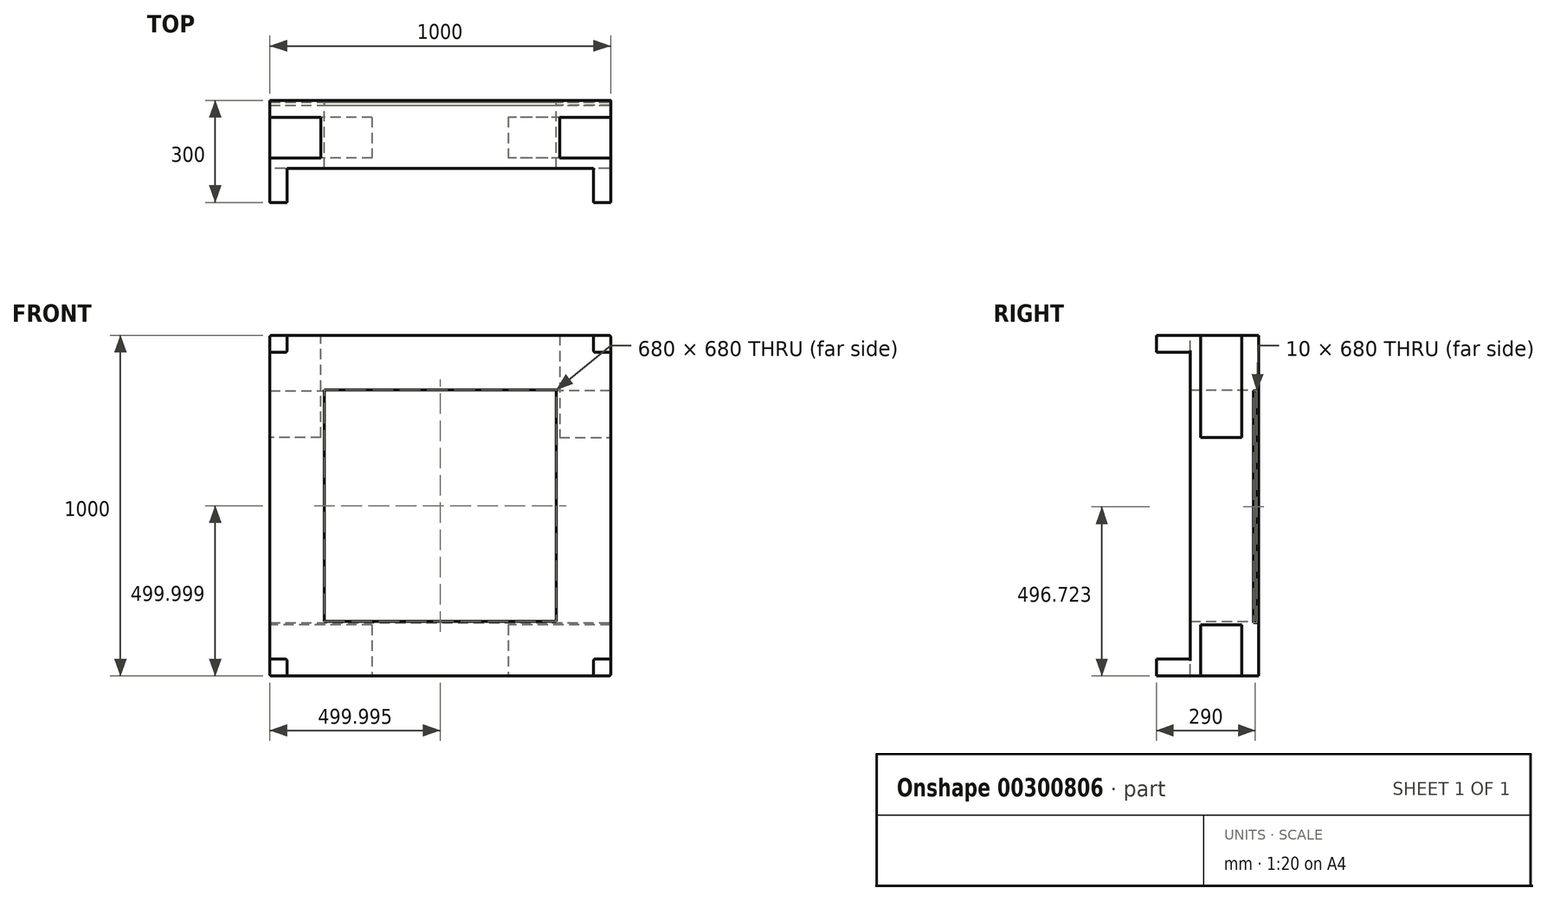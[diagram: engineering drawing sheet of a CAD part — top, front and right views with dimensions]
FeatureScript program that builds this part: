
annotation { "Feature Type Name" : "Feature", "Feature Type Description" : "" }
export const myFeature = defineFeature(function(context is Context, id is Id, definition is map)
    precondition{}
    {
        {
            var Q0;
            Q0=qCreatedBy(makeId("Front.planeOp"),FACE);
            var sketch = newSketch(context, id + "F0", { "sketchPlane" : qUnion([Q0])});
            skLineSegment(sketch, "E0.bottom", {"start": v(-49.23, 948.9) * mm, "end": v(950.77, 948.9) * mm});
            skLineSegment(sketch, "E0.top", {"start": v(-49.23, -51.1) * mm, "end": v(950.77, -51.1) * mm});
            skLineSegment(sketch, "E0.left", {"start": v(-49.23, 948.9) * mm, "end": v(-49.23, -51.1) * mm});
            skLineSegment(sketch, "E0.right", {"start": v(950.77, 948.9) * mm, "end": v(950.77, -51.1) * mm});
            skSolve(sketch);
        }
        {
            var Q0;
            Q0 = qSketchRegion(id + "F0", true);
            extrude(context, id + "F1", {"entities" : qUnion([Q0]), "depth" : 300 * mm});
        }
        {
            var Q0;
            Q0=makeQuery(id+"F1.opExtrude","SWEPT_FACE",FACE,{"disambiguationData":[OSD([sQuery(id+"F0.wireOp",EDGE,"E0.bottom")])]});
            var sketch = newSketch(context, id + "F2", { "sketchPlane" : qUnion([Q0])});
            skLineSegment(sketch, "E1.bottom", {"start": v(0.77, -300) * mm, "end": v(900.77, -300) * mm});
            skLineSegment(sketch, "E1.top", {"start": v(0.77, -200) * mm, "end": v(900.77, -200) * mm});
            skLineSegment(sketch, "E1.left", {"start": v(0.77, -300) * mm, "end": v(0.77, -200) * mm});
            skLineSegment(sketch, "E1.right", {"start": v(900.77, -300) * mm, "end": v(900.77, -200) * mm});
            skSolve(sketch);
        }
        {
            var Q0;
            Q0 = qSketchRegion(id + "F2", true);
            extrude(context, id + "F3", {"entities" : qUnion([Q0]), "operationType" : NewBodyOperationType.REMOVE, "endBound" : BoundingType.THROUGH_ALL, "oppositeDirection" : true, "depth" : 100 * mm});
        }
        {
            var Q0;
            Q0=makeQuery(id+"F1.opExtrude","SWEPT_FACE",FACE,{"disambiguationData":[OSD([sQuery(id+"F0.wireOp",EDGE,"E0.left")])]});
            var sketch = newSketch(context, id + "F4", { "sketchPlane" : qUnion([Q0])});
            skLineSegment(sketch, "E2.bottom", {"start": v(300, -1.1) * mm, "end": v(200, -1.1) * mm});
            skLineSegment(sketch, "E2.top", {"start": v(300, 898.9) * mm, "end": v(200, 898.9) * mm});
            skLineSegment(sketch, "E2.left", {"start": v(300, -1.1) * mm, "end": v(300, 898.9) * mm});
            skLineSegment(sketch, "E2.right", {"start": v(200, -1.1) * mm, "end": v(200, 898.9) * mm});
            skSolve(sketch);
        }
        {
            var Q0;
            Q0 = qSketchRegion(id + "F4", true);
            extrude(context, id + "F5", {"entities" : qUnion([Q0]), "operationType" : NewBodyOperationType.REMOVE, "endBound" : BoundingType.THROUGH_ALL, "oppositeDirection" : true, "depth" : 25 * mm});
        }
        {
            var Q0;
            Q0=makeQuery(id+"F1.opExtrude","SWEPT_FACE",FACE,{"disambiguationData":[OSD([sQuery(id+"F0.wireOp",EDGE,"E0.top")])]});
            var sketch = newSketch(context, id + "F6", { "sketchPlane" : qUnion([Q0])});
            skLineSegment(sketch, "E3.bottom", {"start": v(250.77, 50) * mm, "end": v(-49.23, 50) * mm});
            skLineSegment(sketch, "E3.top", {"start": v(250.77, 170) * mm, "end": v(-49.23, 170) * mm});
            skLineSegment(sketch, "E3.left", {"start": v(250.77, 50) * mm, "end": v(250.77, 170) * mm});
            skLineSegment(sketch, "E3.right", {"start": v(-49.23, 50) * mm, "end": v(-49.23, 170) * mm});
            skSolve(sketch);
        }
        {
            var Q0;
            Q0 = qSketchRegion(id + "F6", true);
            extrude(context, id + "F7", {"entities" : qUnion([Q0]), "operationType" : NewBodyOperationType.REMOVE, "oppositeDirection" : true, "depth" : 150 * mm});
        }
        {
            var Q0;
            Q0=makeQuery(id+"F1.opExtrude","SWEPT_FACE",FACE,{"disambiguationData":[OSD([sQuery(id+"F0.wireOp",EDGE,"E0.top")])]});
            var sketch = newSketch(context, id + "F8", { "sketchPlane" : qUnion([Q0])});
            skLineSegment(sketch, "E4.bottom", {"start": v(950.77, 50) * mm, "end": v(650.77, 50) * mm});
            skLineSegment(sketch, "E4.top", {"start": v(950.77, 170) * mm, "end": v(650.77, 170) * mm});
            skLineSegment(sketch, "E4.left", {"start": v(950.77, 50) * mm, "end": v(950.77, 170) * mm});
            skLineSegment(sketch, "E4.right", {"start": v(650.77, 50) * mm, "end": v(650.77, 170) * mm});
            skSolve(sketch);
        }
        {
            var Q0;
            Q0 = qSketchRegion(id + "F8", true);
            extrude(context, id + "F9", {"entities" : qUnion([Q0]), "operationType" : NewBodyOperationType.REMOVE, "oppositeDirection" : true, "depth" : 150 * mm});
        }
        {
            var Q0;
            Q0=makeQuery(id+"F1.opExtrude","SWEPT_FACE",FACE,{"disambiguationData":[OSD([sQuery(id+"F0.wireOp",EDGE,"E0.right")])]});
            var sketch = newSketch(context, id + "F10", { "sketchPlane" : qUnion([Q0])});
            skLineSegment(sketch, "E5.bottom", {"start": v(-50, 948.9) * mm, "end": v(-170, 948.9) * mm});
            skLineSegment(sketch, "E5.top", {"start": v(-50, 648.9) * mm, "end": v(-170, 648.9) * mm});
            skLineSegment(sketch, "E5.left", {"start": v(-50, 948.9) * mm, "end": v(-50, 648.9) * mm});
            skLineSegment(sketch, "E5.right", {"start": v(-170, 948.9) * mm, "end": v(-170, 648.9) * mm});
            skSolve(sketch);
        }
        {
            var Q0;
            Q0 = qSketchRegion(id + "F10", true);
            extrude(context, id + "F11", {"entities" : qUnion([Q0]), "operationType" : NewBodyOperationType.REMOVE, "oppositeDirection" : true, "depth" : 150 * mm});
        }
        {
            var Q0;
            Q0=makeQuery(id+"F1.opExtrude","SWEPT_FACE",FACE,{"disambiguationData":[OSD([sQuery(id+"F0.wireOp",EDGE,"E0.left")])]});
            var sketch = newSketch(context, id + "F12", { "sketchPlane" : qUnion([Q0])});
            skLineSegment(sketch, "E6.bottom", {"start": v(50, 648.9) * mm, "end": v(170, 648.9) * mm});
            skLineSegment(sketch, "E6.top", {"start": v(50, 948.9) * mm, "end": v(170, 948.9) * mm});
            skLineSegment(sketch, "E6.left", {"start": v(50, 648.9) * mm, "end": v(50, 948.9) * mm});
            skLineSegment(sketch, "E6.right", {"start": v(170, 648.9) * mm, "end": v(170, 948.9) * mm});
            skSolve(sketch);
        }
        {
            var Q0;
            Q0 = qSketchRegion(id + "F12", true);
            extrude(context, id + "F13", {"entities" : qUnion([Q0]), "operationType" : NewBodyOperationType.REMOVE, "oppositeDirection" : true, "depth" : 150 * mm});
        }
        {
            var Q0;
            {var subQ0=sQuery(id+"F0.wireOp",EDGE,"E0.right");var subQ1=sQuery(id+"F0.wireOp",EDGE,"E0.top");Q0=makeQuery(id+"F9.boolean.opBoolean","SPLIT",EDGE,{"disambiguationData":[TD([makeQuery(id+"F9.opExtrude","SWEPT_FACE",FACE,{"disambiguationData":[OSD([sQuery(id+"F8.wireOp",EDGE,"E4.top")])]})])],"derivedFrom":makeQuery(id+"F1.opExtrude","SWEPT_EDGE",EDGE,{"disambiguationData":[OSD([subQ1,subQ0])]})});}
            var Q1;
            Q1=makeQuery(id+"F3.boolean.opBoolean","INTERSECT",EDGE,{"derivedFrom":[makeQuery(id+"F1.opExtrude","SWEPT_FACE",FACE,{"disambiguationData":[OSD([sQuery(id+"F0.wireOp",EDGE,"E0.top")])]}),makeQuery(id+"F3.opExtrude","SWEPT_FACE",FACE,{"disambiguationData":[OSD([sQuery(id+"F2.wireOp",EDGE,"E1.right")])]})]});
            var Q2;
            Q2=makeQuery(id+"F5.boolean.opBoolean","INTERSECT",EDGE,{"derivedFrom":[makeQuery(id+"F1.opExtrude","SWEPT_FACE",FACE,{"disambiguationData":[OSD([sQuery(id+"F0.wireOp",EDGE,"E0.right")])]}),makeQuery(id+"F5.opExtrude","SWEPT_FACE",FACE,{"disambiguationData":[OSD([sQuery(id+"F4.wireOp",EDGE,"E2.bottom")])]})]});
            var Q3;
            Q3=makeQuery(id+"F5.boolean.opBoolean","INTERSECT",EDGE,{"derivedFrom":[makeQuery(id+"F3.boolean.opBoolean","COPY",FACE,{"derivedFrom":makeQuery(id+"F3.opExtrude","SWEPT_FACE",FACE,{"disambiguationData":[OSD([sQuery(id+"F2.wireOp",EDGE,"E1.right")])]})}),makeQuery(id+"F5.opExtrude","SWEPT_FACE",FACE,{"disambiguationData":[OSD([sQuery(id+"F4.wireOp",EDGE,"E2.bottom")])]})]});
            var Q4;
            {var subQ0=sQuery(id+"F0.wireOp",EDGE,"E0.left");var subQ1=sQuery(id+"F0.wireOp",EDGE,"E0.top");Q4=makeQuery(id+"F7.boolean.opBoolean","SPLIT",EDGE,{"disambiguationData":[TD([makeQuery(id+"F7.opExtrude","SWEPT_FACE",FACE,{"disambiguationData":[OSD([sQuery(id+"F6.wireOp",EDGE,"E3.top")])]})])],"derivedFrom":makeQuery(id+"F1.opExtrude","SWEPT_EDGE",EDGE,{"disambiguationData":[OSD([subQ1,subQ0])]})});}
            var Q5;
            Q5=makeQuery(id+"F3.boolean.opBoolean","INTERSECT",EDGE,{"derivedFrom":[makeQuery(id+"F1.opExtrude","SWEPT_FACE",FACE,{"disambiguationData":[OSD([sQuery(id+"F0.wireOp",EDGE,"E0.top")])]}),makeQuery(id+"F3.opExtrude","SWEPT_FACE",FACE,{"disambiguationData":[OSD([sQuery(id+"F2.wireOp",EDGE,"E1.left")])]})]});
            var Q6;
            Q6=makeQuery(id+"F5.boolean.opBoolean","COPY",EDGE,{"derivedFrom":makeQuery(id+"F5.opExtrude","CAP_EDGE",EDGE,{"disambiguationData":[OSD([sQuery(id+"F4.wireOp",EDGE,"E2.bottom")])],"isStart":true})});
            var Q7;
            Q7=makeQuery(id+"F5.boolean.opBoolean","INTERSECT",EDGE,{"derivedFrom":[makeQuery(id+"F3.boolean.opBoolean","COPY",FACE,{"derivedFrom":makeQuery(id+"F3.opExtrude","SWEPT_FACE",FACE,{"disambiguationData":[OSD([sQuery(id+"F2.wireOp",EDGE,"E1.left")])]})}),makeQuery(id+"F5.opExtrude","SWEPT_FACE",FACE,{"disambiguationData":[OSD([sQuery(id+"F4.wireOp",EDGE,"E2.bottom")])]})]});
            var Q8;
            {var subQ0=sQuery(id+"F0.wireOp",EDGE,"E0.bottom");var subQ1=sQuery(id+"F0.wireOp",EDGE,"E0.left");Q8=makeQuery(id+"F13.boolean.opBoolean","SPLIT",EDGE,{"disambiguationData":[TD([makeQuery(id+"F13.opExtrude","SWEPT_FACE",FACE,{"disambiguationData":[OSD([sQuery(id+"F12.wireOp",EDGE,"E6.right")])]})])],"derivedFrom":makeQuery(id+"F1.opExtrude","SWEPT_EDGE",EDGE,{"disambiguationData":[OSD([subQ0,subQ1])]})});}
            var Q9;
            Q9=makeQuery(id+"F3.boolean.opBoolean","COPY",EDGE,{"derivedFrom":makeQuery(id+"F3.opExtrude","CAP_EDGE",EDGE,{"disambiguationData":[OSD([sQuery(id+"F2.wireOp",EDGE,"E1.left")])],"isStart":true})});
            var Q10;
            Q10=makeQuery(id+"F5.boolean.opBoolean","COPY",EDGE,{"derivedFrom":makeQuery(id+"F5.opExtrude","CAP_EDGE",EDGE,{"disambiguationData":[OSD([sQuery(id+"F4.wireOp",EDGE,"E2.top")])],"isStart":true})});
            var Q11;
            Q11=makeQuery(id+"F5.boolean.opBoolean","INTERSECT",EDGE,{"derivedFrom":[makeQuery(id+"F3.boolean.opBoolean","COPY",FACE,{"derivedFrom":makeQuery(id+"F3.opExtrude","SWEPT_FACE",FACE,{"disambiguationData":[OSD([sQuery(id+"F2.wireOp",EDGE,"E1.left")])]})}),makeQuery(id+"F5.opExtrude","SWEPT_FACE",FACE,{"disambiguationData":[OSD([sQuery(id+"F4.wireOp",EDGE,"E2.top")])]})]});
            var Q12;
            {var subQ0=sQuery(id+"F0.wireOp",EDGE,"E0.bottom");var subQ1=sQuery(id+"F0.wireOp",EDGE,"E0.right");Q12=makeQuery(id+"F11.boolean.opBoolean","SPLIT",EDGE,{"disambiguationData":[TD([makeQuery(id+"F11.opExtrude","SWEPT_FACE",FACE,{"disambiguationData":[OSD([sQuery(id+"F10.wireOp",EDGE,"E5.right")])]})])],"derivedFrom":makeQuery(id+"F1.opExtrude","SWEPT_EDGE",EDGE,{"disambiguationData":[OSD([subQ0,subQ1])]})});}
            var Q13;
            Q13=makeQuery(id+"F5.boolean.opBoolean","INTERSECT",EDGE,{"derivedFrom":[makeQuery(id+"F1.opExtrude","SWEPT_FACE",FACE,{"disambiguationData":[OSD([sQuery(id+"F0.wireOp",EDGE,"E0.right")])]}),makeQuery(id+"F5.opExtrude","SWEPT_FACE",FACE,{"disambiguationData":[OSD([sQuery(id+"F4.wireOp",EDGE,"E2.top")])]})]});
            var Q14;
            Q14=makeQuery(id+"F5.boolean.opBoolean","INTERSECT",EDGE,{"derivedFrom":[makeQuery(id+"F3.boolean.opBoolean","COPY",FACE,{"derivedFrom":makeQuery(id+"F3.opExtrude","SWEPT_FACE",FACE,{"disambiguationData":[OSD([sQuery(id+"F2.wireOp",EDGE,"E1.right")])]})}),makeQuery(id+"F5.opExtrude","SWEPT_FACE",FACE,{"disambiguationData":[OSD([sQuery(id+"F4.wireOp",EDGE,"E2.top")])]})]});
            var Q15;
            Q15=makeQuery(id+"F3.boolean.opBoolean","COPY",EDGE,{"derivedFrom":makeQuery(id+"F3.opExtrude","CAP_EDGE",EDGE,{"disambiguationData":[OSD([sQuery(id+"F2.wireOp",EDGE,"E1.right")])],"isStart":true})});
            fillet(context, id + "F14", {"entities" : qUnion([Q0, Q1, Q2, Q3, Q4, Q5, Q6, Q7, Q8, Q9, Q10, Q11, Q12, Q13, Q14, Q15]), "radius" : 5 * mm, "tangentPropagation" : true, "allowEdgeOverflow" : false});
        }
        {
            var Q0;
            {var subQ0=sQuery(id+"F0.wireOp",EDGE,"E0.bottom");var subQ1=sQuery(id+"F0.wireOp",EDGE,"E0.right");Q0=makeQuery(id+"F11.boolean.opBoolean","SPLIT",EDGE,{"disambiguationData":[TD([makeQuery(id+"F11.opExtrude","SWEPT_FACE",FACE,{"disambiguationData":[OSD([sQuery(id+"F10.wireOp",EDGE,"E5.left")])]})])],"derivedFrom":makeQuery(id+"F1.opExtrude","SWEPT_EDGE",EDGE,{"disambiguationData":[OSD([subQ0,subQ1])]})});}
            var Q1;
            {var subQ0=sQuery(id+"F0.wireOp",EDGE,"E0.right");var subQ1=sQuery(id+"F0.wireOp",EDGE,"E0.top");Q1=makeQuery(id+"F9.boolean.opBoolean","SPLIT",EDGE,{"disambiguationData":[TD([makeQuery(id+"F9.opExtrude","SWEPT_FACE",FACE,{"disambiguationData":[OSD([sQuery(id+"F8.wireOp",EDGE,"E4.bottom")])]})])],"derivedFrom":makeQuery(id+"F1.opExtrude","SWEPT_EDGE",EDGE,{"disambiguationData":[OSD([subQ1,subQ0])]})});}
            var Q2;
            {var subQ0=sQuery(id+"F0.wireOp",EDGE,"E0.left");var subQ1=sQuery(id+"F0.wireOp",EDGE,"E0.top");Q2=makeQuery(id+"F7.boolean.opBoolean","SPLIT",EDGE,{"disambiguationData":[TD([makeQuery(id+"F7.opExtrude","SWEPT_FACE",FACE,{"disambiguationData":[OSD([sQuery(id+"F6.wireOp",EDGE,"E3.bottom")])]})])],"derivedFrom":makeQuery(id+"F1.opExtrude","SWEPT_EDGE",EDGE,{"disambiguationData":[OSD([subQ1,subQ0])]})});}
            var Q3;
            {var subQ0=sQuery(id+"F0.wireOp",EDGE,"E0.bottom");var subQ1=sQuery(id+"F0.wireOp",EDGE,"E0.left");Q3=makeQuery(id+"F13.boolean.opBoolean","SPLIT",EDGE,{"disambiguationData":[TD([makeQuery(id+"F13.opExtrude","SWEPT_FACE",FACE,{"disambiguationData":[OSD([sQuery(id+"F12.wireOp",EDGE,"E6.left")])]})])],"derivedFrom":makeQuery(id+"F1.opExtrude","SWEPT_EDGE",EDGE,{"disambiguationData":[OSD([subQ0,subQ1])]})});}
            fillet(context, id + "F15", {"entities" : qUnion([Q0, Q1, Q2, Q3]), "radius" : 5 * mm, "tangentPropagation" : true, "allowEdgeOverflow" : false});
        }
        {
            var Q0;
            Q0=makeQuery(id+"F1.opExtrude","CAP_FACE",FACE,{"disambiguationData":[OSD([sQuery(id+"F0.wireOp",EDGE,"E0.bottom"),sQuery(id+"F0.wireOp",EDGE,"E0.top"),sQuery(id+"F0.wireOp",EDGE,"E0.left"),sQuery(id+"F0.wireOp",EDGE,"E0.right")])],"isStart":true});
            var sketch = newSketch(context, id + "F16", { "sketchPlane" : qUnion([Q0])});
            skLineSegment(sketch, "E7.bottom", {"start": v(-790.77, 788.9) * mm, "end": v(-110.77, 788.9) * mm});
            skLineSegment(sketch, "E7.top", {"start": v(-790.77, 108.9) * mm, "end": v(-110.77, 108.9) * mm});
            skLineSegment(sketch, "E7.left", {"start": v(-790.77, 788.9) * mm, "end": v(-790.77, 108.9) * mm});
            skLineSegment(sketch, "E7.right", {"start": v(-110.77, 788.9) * mm, "end": v(-110.77, 108.9) * mm});
            skSolve(sketch);
        }
        {
            var Q0;
            Q0 = qSketchRegion(id + "F16", true);
            extrude(context, id + "F17", {"entities" : qUnion([Q0]), "operationType" : NewBodyOperationType.REMOVE, "endBound" : BoundingType.THROUGH_ALL, "oppositeDirection" : true, "depth" : 25 * mm});
        }
        {
            var Q0;
            Q0=makeQuery(id+"F17.boolean.opBoolean","COPY",FACE,{"derivedFrom":makeQuery(id+"F17.opExtrude","SWEPT_FACE",FACE,{"disambiguationData":[OSD([sQuery(id+"F16.wireOp",EDGE,"E7.right")])]})});
            var sketch = newSketch(context, id + "F18", { "sketchPlane" : qUnion([Q0])});
            skLineSegment(sketch, "E8.bottom", {"start": v(-5, 785.62) * mm, "end": v(-15, 785.62) * mm});
            skLineSegment(sketch, "E8.top", {"start": v(-5, 105.62) * mm, "end": v(-15, 105.62) * mm});
            skLineSegment(sketch, "E8.left", {"start": v(-5, 785.62) * mm, "end": v(-5, 105.62) * mm});
            skLineSegment(sketch, "E8.right", {"start": v(-15, 785.62) * mm, "end": v(-15, 105.62) * mm});
            skSolve(sketch);
        }
        {
            var Q0;
            Q0 = qSketchRegion(id + "F18", true);
            extrude(context, id + "F19", {"entities" : qUnion([Q0]), "operationType" : NewBodyOperationType.REMOVE, "endBound" : BoundingType.THROUGH_ALL, "oppositeDirection" : true, "depth" : 25 * mm});
        }
        {
            var Q0;
            Q0 = qSketchRegion(id + "F18", true);
            extrude(context, id + "F20", {"entities" : qUnion([Q0]), "operationType" : NewBodyOperationType.REMOVE, "endBound" : BoundingType.THROUGH_ALL, "depth" : 25 * mm});
        }
    });
